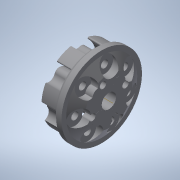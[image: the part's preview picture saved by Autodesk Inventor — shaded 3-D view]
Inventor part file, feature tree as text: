
AUTODESK INVENTOR PART (.ipt)
format: ipt  version: 2020 (Build 240168000, 168)  size: 637,952 bytes
history: native  units: in
note: dims shown in document units (in); Inventor stores cm internally (conversion verified against a paired STEP export)
features: other x4, sketch x4, extrude x2, plane x2
ambient origin geometry x8: Origin, YZ Plane, XZ Plane, XY Plane, X Axis, Y Axis, Z Axis, Center Point
bodies: Solid1 (feature_tree)
feature tree (12):
  other  "Mecanum Adaptor 1.3.ipt"
  extrude  "Extrusion1"  Depth=0.217in TaperAngle=0.0deg
  extrude  "Extrusion2"  Depth=0.1406in
  other  "Solid1::Mecanum Adaptor 1.3.ipt"
  other  "TaggingFeature1"
  sketch  "Sketch6"  dims[d0=0.3937in]
  sketch  "Sketch11"  dims[d4=0.4724in d5=0.0in d6=0.0787in d7=1.757in d8=1.6061in d9=0.0in d10=90.0deg d11=0.0in d12=90.0deg d13=0.1181in d14=0.0in d15=0.1575in d16=2.7559in d21=0.0in d23=0.0in d25=0.0in d26=0.1575in d27=0.0in d28=0.374in d29=2.7559in d33=0.0787in d34=0.0in d35=0.1378in d36=0.0in d38=0.0in d55=2.7559in d60=0.0in d61=0.2756in d62=0.7874in d64=0.446in d65=0.7874in d67=0.446in d70=0.0984in d71=0.0in d72=0.2638in d73=0.1575in d75=0.2638in d76=0.1575in d78=0.2638in d79=0.1575in d81=0.2638in d82=0.1575in d84=0.2638in d85=0.1575in d87=0.2638in d88=0.1575in d90=0.2638in d91=0.1575in d93=0.1575in d2=360.0deg d18=360.0deg d31=360.0deg d57=360.0deg d1=0.217in d3=0.0in]
  plane  "Work Plane1"
  plane  "Work Plane2"
  other  "Work Axis1"
  sketch  "Sketch18"  dims[d19=0.1406in d20=0.1406in]
  sketch  "Sketch19"  dims[d22=0.1406in d24=0.1406in d30=0.7795in d32=0.0in]
